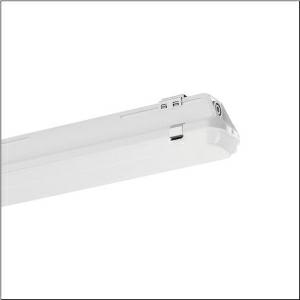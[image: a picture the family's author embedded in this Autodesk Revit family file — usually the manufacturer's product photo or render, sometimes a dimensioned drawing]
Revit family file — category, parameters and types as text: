
# Revit family: monsun_r__21_51fb107p460b005_4f74
name_source: partatom
category: Lighting Fixtures
units: mm (PartAtom-declared; Revit-internal decimal feet)

## family parameters
Cut with Voids When Loaded = No
Host = Face
Light Source = No
Part Type = Normal
Room Calculation Point = No
Round Connector Dimension = Use Diameter
Shared = No

## types (1)
- Monsun® 21 (1 x LED, 6000 lm, 38 W, 4000K)
    Apparent Load = 38 VA
    CIE Flux Codes = 47 77 93 94 100
    Color Rendering = 80
    Color Temperature = 4000K
    Default Elevation = 1800 mm
    Description = Monsun® 21, damp-proof luminaire, chain hanger, primary optical cover: enclosure, of PMMA, light emission: direct distribution, primary light characteristic: symmetric, installation type: suspended mounting, surface-mounted, horizontal mounting, vertical mounting, LED, rated luminous flux: 6.000lm, luminous efficacy: 158lm/W, light colour: 840, colour temperature: 4000K, control gear: ECG, with terminal, 3-pole, max. 2.5mm², through-wiring: 5x 2.5mm², mains connection: 220..240V, AC, 50/60Hz, rated input power: 38W, housing, of glass-fibre reinforced polyester, uncoated, bright grey, length: 1.590mm, width: 90mm, height: 88mm, clip for enclosure, of stainless steel (V2A), ceiling mounting element, of stainless steel (V2A), chain hanger, of stainless steel (V2A), protection rating (complete): IP66, insulation class (complete): insulation class I (protective earthing), certification: CE, ENEC, VDE, UKCA, protection symbol: D, impact resistance: IK04, permissible operating ambient temperature: -25..+35°C, standard: EN 50419, EN 60598-2-1, corresponds to IFS (International Featured Standards) requirements for safety and quality in the food industry, for indoor or canopied outdoor use, no direct snow, no direct sun, no direct rain, packaging unit: 1 piece
    Height = 89 mm
    Lamp = 1 x LED
    Lamp Light Flux = 6000 lm
    Lamp Power = 38 W
    Lamp count = 1
    Length = 1590 mm
    Luminous efficacy = 158 lm/W
    Manufacturer = Siteco
    ModVariant = No
    Model = 51FB107P460B005
    Mounting Place = Ceiling
    Mounting Type = Pendant
    Number of Poles = 1
    OnlyDefault = Yes
    Power Factor = 1
    Product Name = Monsun® 21
    Product group = damp-proof luminaire | ceiling pendant
    ProductGroupID = 908
    Protection Class = Protection class I
    Protection Degree = IP 66
    RLX_Detail_Level = 1
    RlxData = <blob elided: 88277 chars, md5=cf295663>
    Socket = socket
    Standby Power = 0 W
    System Light Flux = 6000 lm
    System Power = 38 W
    Type Comments = Product without accessories
    Type Image = l_1006717.jpg
    URL = http://relux.com
    VarID = ---
    Voltage = 0 V
    Weight = 0.00 kg
    Width = 90 mm

## geometry (parser evidence)
native form markers: Blend x4, Sweep x13
no freeform markers — native parametric forms only
